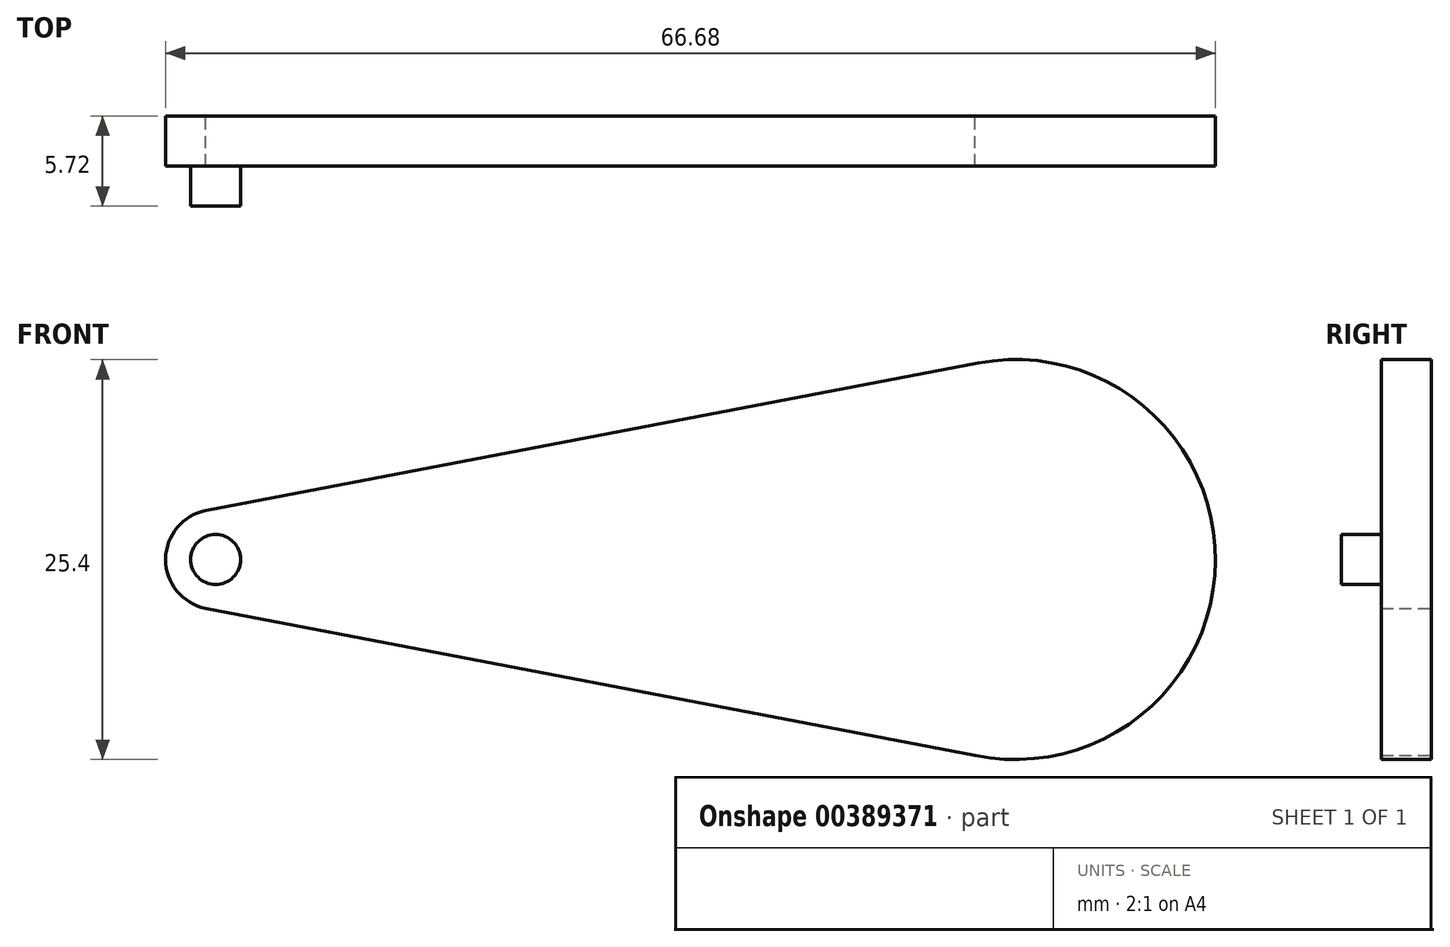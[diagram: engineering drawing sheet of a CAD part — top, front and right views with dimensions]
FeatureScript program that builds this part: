
annotation { "Feature Type Name" : "Feature", "Feature Type Description" : "" }
export const myFeature = defineFeature(function(context is Context, id is Id, definition is map)
    precondition{}
    {
        {
            var Q0;
            Q0=qCreatedBy(makeId("Front.planeOp"),FACE);
            var sketch = newSketch(context, id + "F0", { "sketchPlane" : qUnion([Q0])});
            skArc(sketch, "E0", {"start": v(-0.6, 3.12) * mm, "mid": v(-3.17, 0.02) * mm, "end": v(-0.64, -3.1) * mm});
            skArc(sketch, "E1", {"start": v(48.23, -12.44) * mm, "mid": v(63.5, -0.1) * mm, "end": v(48.42, 12.47) * mm});
            skLineSegment(sketch, "E2", {"start": v(-0.6, 3.12) * mm, "end": v(48.42, 12.47) * mm});
            skPoint(sketch, "E3.orphan", {"position": v(-16.93, 0) * mm});
            skLineSegment(sketch, "E4.trimOffspring", {"start": v(-0.64, -3.1) * mm, "end": v(48.23, -12.44) * mm});
            skSolve(sketch);
        }
        {
            var Q0;
            Q0=makeQuery(id+"F0.imprint","IMPRINT",FACE,{"disambiguationData":[TD([[makeQuery(id+"F0.imprint","IMPRINT",EDGE,{"derivedFrom":sQuery(id+"F0.wireOp",EDGE,"E0")}),1.0]])]});
            extrude(context, id + "F1", {"entities" : qUnion([Q0]), "depth" : 3.17 * mm});
        }
        {
            var Q0;
            Q0=makeQuery(id+"F1.opExtrude","CAP_FACE",FACE,{"disambiguationData":[OSD([sQuery(id+"F0.wireOp",EDGE,"E0"),sQuery(id+"F0.wireOp",EDGE,"E1"),sQuery(id+"F0.wireOp",EDGE,"E2"),sQuery(id+"F0.wireOp",EDGE,"E4.trimOffspring")])],"isStart":false});
            var sketch = newSketch(context, id + "F2", { "sketchPlane" : qUnion([Q0])});
            skCircle(sketch, "E5", {"center": v(0, 0) * mm, "radius": 1.59 * mm});
            skSolve(sketch);
        }
        {
            var Q0;
            Q0 = qSketchRegion(id + "F2", true);
            extrude(context, id + "F3", {"entities" : qUnion([Q0]), "operationType" : NewBodyOperationType.ADD, "depth" : 2.54 * mm});
        }
    });
